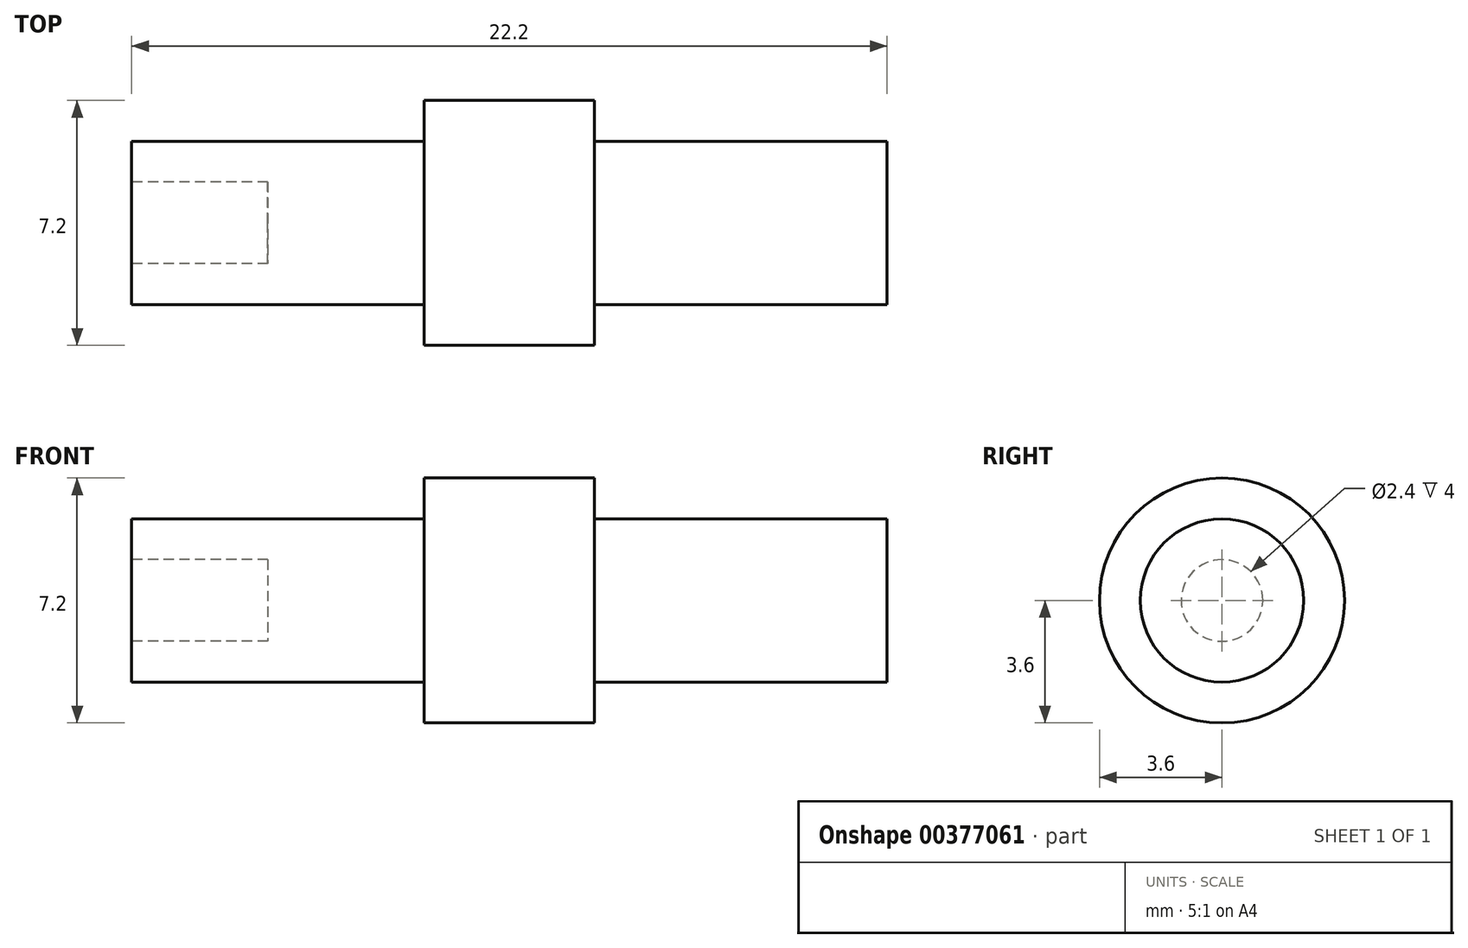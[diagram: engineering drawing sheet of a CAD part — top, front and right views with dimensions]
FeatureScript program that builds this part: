
annotation { "Feature Type Name" : "Feature", "Feature Type Description" : "" }
export const myFeature = defineFeature(function(context is Context, id is Id, definition is map)
    precondition{}
    {
        {
            var Q0;
            Q0=qCreatedBy(makeId("Front.planeOp"),FACE);
            var sketch = newSketch(context, id + "F0", { "sketchPlane" : qUnion([Q0])});
            skLineSegment(sketch, "E0", {"start": v(0, 3.6) * mm, "end": v(5, 3.6) * mm});
            skLineSegment(sketch, "E1", {"start": v(5, 3.6) * mm, "end": v(5, 2.4) * mm});
            skLineSegment(sketch, "E2", {"start": v(5, 2.4) * mm, "end": v(13.6, 2.4) * mm});
            skLineSegment(sketch, "E3", {"start": v(-8.6, 2.4) * mm, "end": v(0, 2.4) * mm});
            skLineSegment(sketch, "E4", {"start": v(0, 2.4) * mm, "end": v(0, 3.6) * mm});
            skLineSegment(sketch, "E5", {"start": v(-8.6, 2.4) * mm, "end": v(-8.6, 1.2) * mm});
            skLineSegment(sketch, "E6", {"start": v(-8.6, 1.2) * mm, "end": v(-4.6, 1.2) * mm});
            skLineSegment(sketch, "E7", {"start": v(13.6, 0) * mm, "end": v(13.6, 2.4) * mm});
            skLineSegment(sketch, "E8", {"start": v(-4.6, 1.2) * mm, "end": v(-4.6, 0) * mm});
            skLineSegment(sketch, "E9", {"start": v(-4.6, 0) * mm, "end": v(13.6, 0) * mm});
            skSolve(sketch);
        }
        {
            var Q0;
            Q0 = qSketchRegion(id + "F0", true);
            var Q1;
            Q1=sQuery(id+"F0.wireOp",EDGE,"E9");
            revolve(context, id + "F1", {"entities" : qUnion([Q0]), "axis" : qUnion([Q1]), "revolveType" : RevolveType.FULL});
        }
    });
